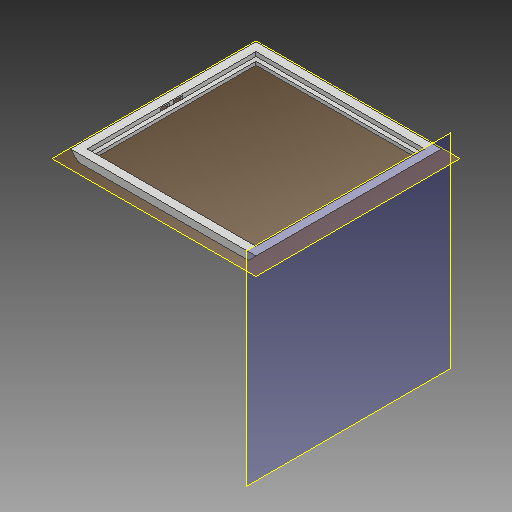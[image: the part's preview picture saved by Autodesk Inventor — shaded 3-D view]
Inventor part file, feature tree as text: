
AUTODESK INVENTOR PART (.ipt)
format: ipt  version: 2018.3 (Build 223284000, 284)  size: 208,384 bytes
history: native  units: mm
features: reference x20, other x12, extrude x6, sketch x6, plane x2, chamfer x1, projected_geometry x1
ambient origin geometry x8: Origin, YZ Plane, XZ Plane, XY Plane, X Axis, Y Axis, Z Axis, Center Point
bodies: Volumenkörper1 (feature_tree)
feature tree (48):
  extrude  "Extrusion1"  [1 undecoded]
  plane  "Arbeitsebene1"
  extrude  "Extrusion2"  Depth=10.0mm
  extrude  "Extrusion3"  Depth=10.0mm
  plane  "Arbeitsebene3"
  extrude  "Extrusion4"  Depth=8.0mm TaperAngle=0.0deg
  extrude  "Extrusion5"  Depth=2.0mm TaperAngle=0.0deg
  extrude  "Extrusion6"  Depth=18.0mm TaperAngle=45.0deg
  chamfer  "Fase2"  [1 undecoded]
  sketch  "Skizze1"  dims[d0=18.0mm d1=0.0mm d5=-20.0mm]
  reference  "Referenz1"
  reference  "Referenz2"
  reference  "Referenz3"
  reference  "Referenz4"
  reference  "Referenz5"
  sketch  "Skizze3"  dims[d6=17.0mm d7=0.0mm d8=10.0mm]
  reference  "Referenz12"
  reference  "Referenz13"
  reference  "Referenz14"
  reference  "Referenz15"
  reference  "Referenz16"
  reference  "Referenz17"
  reference  "Referenz18"
  reference  "Referenz19"
  sketch  "Skizze5"  dims[d9=10.0mm d10=10.0mm]
  sketch  "Skizze6"  dims[d11=10.0mm d12=8.0mm d13=0.0mm]
  reference  "Referenz20"
  reference  "Referenz21"
  reference  "Referenz22"
  reference  "Referenz23"
  reference  "Referenz24"
  reference  "Referenz25"
  sketch  "Skizze7"  dims[d14=25.0mm d15=0.0mm d16=2.0mm d17=0.0mm]
  projected_geometry  "Projizierte Kontur1"
  sketch  "Skizze8"  dims[d18=2.0mm d19=0.0mm d20=18.0mm d21=2.0mm d22=45.0deg]
  reference  "Referenz26"
  parser-record x2  (decoder bookkeeping rows leaked as tree rows — omitted from the tree; the rows remain in map.json)
  other  "SmartCube_Quadratisch.iam"
  other  "Wand2_MIR:1"
  other  "Wand1:1"
  other  "Wand1_MIR:1"
  other  "Wand2:1"
  other  "PV_Modul:1"
  other  "<userpath>\Documents\Dipl\Smartcube_Construction\Version_3\Baugruppe1.iam"
  other  "Baugruppe1.iam"
  other  "PV_Ramen_CPY_3_2:1"
  other  "PV_Modul_CPY_3_CPY2:1"
note: 2 required parameter values undecoded (feature->parameter linkage not recoverable at this tier; creation-order binding heuristic only, values carry confidence <= 0.55)
note: 2 file-system paths scrubbed to <path> (originals preserved in map.json)
